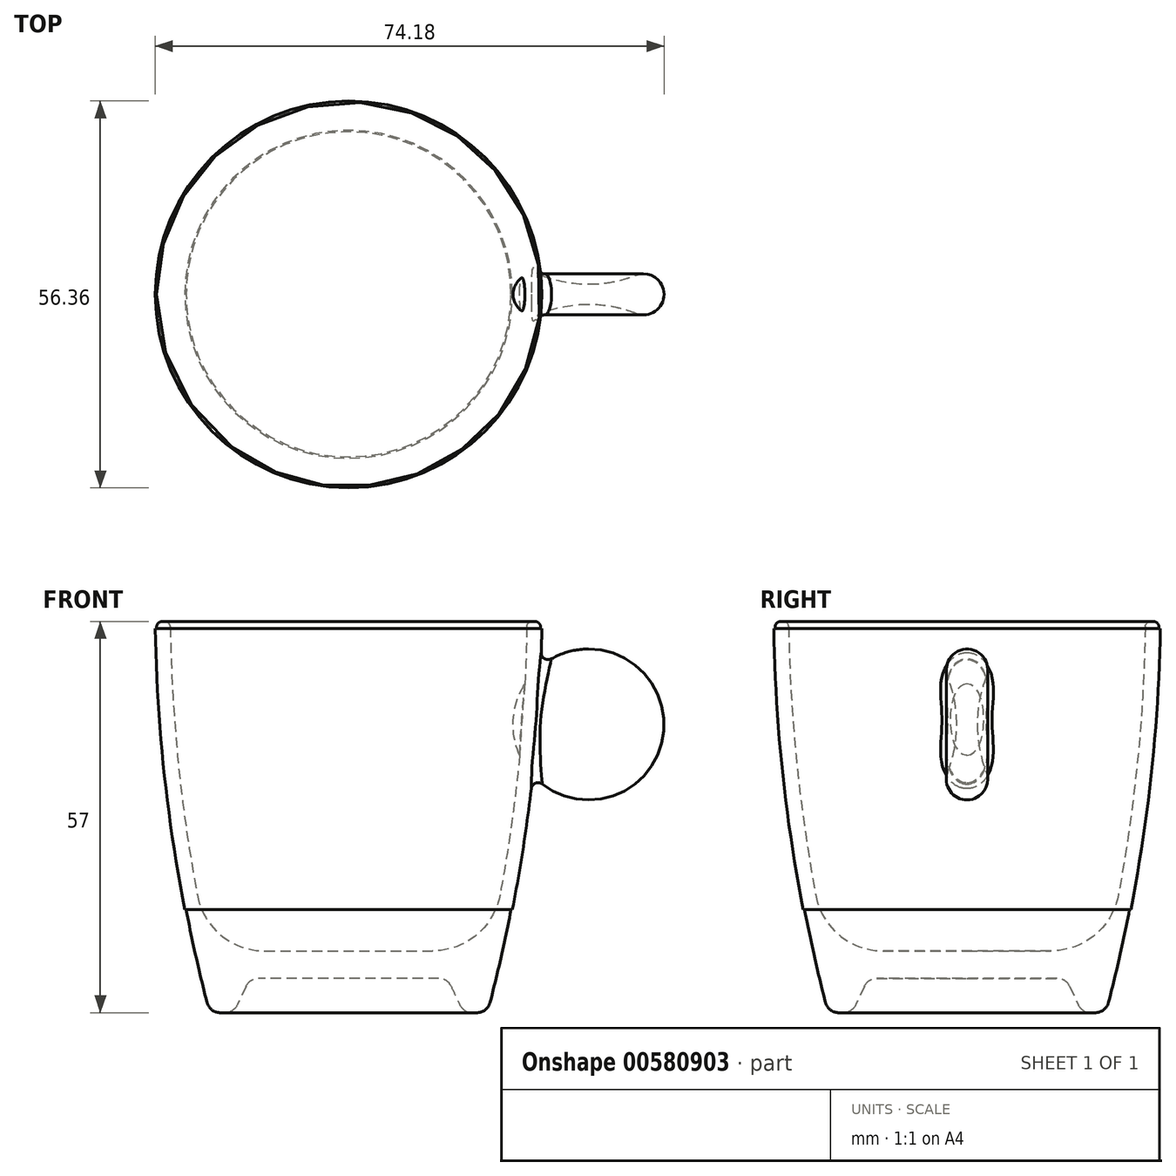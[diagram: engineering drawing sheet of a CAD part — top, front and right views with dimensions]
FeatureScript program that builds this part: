
annotation { "Feature Type Name" : "Feature", "Feature Type Description" : "" }
export const myFeature = defineFeature(function(context is Context, id is Id, definition is map)
    precondition{}
    {
        {
            var Q0;
            Q0=qCreatedBy(makeId("Front.planeOp"),FACE);
            var sketch = newSketch(context, id + "F0", { "sketchPlane" : qUnion([Q0])});
            skLineSegment(sketch, "E0", {"start": v(0, 5) * mm, "end": v(14.42, 5) * mm});
            skLineSegment(sketch, "E1", {"start": v(14.42, 5) * mm, "end": v(16.75, 0) * mm});
            skLineSegment(sketch, "E2", {"start": v(16.75, 0) * mm, "end": v(20.25, 0) * mm});
            skArc(sketch, "E3", {"start": v(20.25, 0) * mm, "mid": v(25.88, 28.26) * mm, "end": v(28, 57) * mm});
            skLineSegment(sketch, "E4", {"start": v(28, 57) * mm, "end": v(26, 57) * mm});
            skLineSegment(sketch, "E5", {"start": v(0, 9) * mm, "end": v(0, 5) * mm});
            skLineSegment(sketch, "E6", {"start": v(20.39, 9) * mm, "end": v(0, 9) * mm});
            skArc(sketch, "E7.trimOffspring", {"start": v(20.39, 9) * mm, "mid": v(24.45, 32.85) * mm, "end": v(26, 57) * mm});
            skPoint(sketch, "E8.orphan", {"position": v(0, 57) * mm});
            skSolve(sketch);
        }
        {
            var Q0;
            Q0=qSketchRegion(id+"F0",true);
            var Q1;
            Q1=sQuery(id+"F0.wireOp",EDGE,"E5");
            revolve(context, id + "F1", {"entities" : qUnion([Q0]), "axis" : qUnion([Q1]), "revolveType" : RevolveType.FULL});
        }
        {
            var Q0;
            Q0=makeQuery(id+"F1.opRevolve","SWEPT_EDGE",EDGE,{"disambiguationData":[OSD([sQuery(id+"F0.wireOp",EDGE,"E4"),sQuery(id+"F0.wireOp",EDGE,"E7.trimOffspring")])]});
            var Q1;
            Q1=makeQuery(id+"F1.opRevolve","SWEPT_EDGE",EDGE,{"disambiguationData":[OSD([sQuery(id+"F0.wireOp",EDGE,"E3"),sQuery(id+"F0.wireOp",EDGE,"E4")])]});
            fillet(context, id + "F2", {"entities" : qUnion([Q0, Q1]), "radius" : .8 * mm, "tangentPropagation" : true, "allowEdgeOverflow" : false});
        }
        {
            var Q0;
            Q0=makeQuery(id+"F1.opRevolve","SWEPT_EDGE",EDGE,{"disambiguationData":[OSD([sQuery(id+"F0.wireOp",EDGE,"E2"),sQuery(id+"F0.wireOp",EDGE,"E3")])]});
            var Q1;
            Q1=makeQuery(id+"F1.opRevolve","SWEPT_EDGE",EDGE,{"disambiguationData":[OSD([sQuery(id+"F0.wireOp",EDGE,"E1"),sQuery(id+"F0.wireOp",EDGE,"E2")])]});
            var Q2;
            Q2=makeQuery(id+"F1.opRevolve","SWEPT_EDGE",EDGE,{"disambiguationData":[OSD([sQuery(id+"F0.wireOp",EDGE,"E0"),sQuery(id+"F0.wireOp",EDGE,"E1")])]});
            fillet(context, id + "F3", {"entities" : qUnion([Q0, Q1, Q2]), "radius" : 2 * mm, "tangentPropagation" : true, "allowEdgeOverflow" : false});
        }
        {
            var Q0;
            Q0=makeQuery(id+"F1.opRevolve","SWEPT_EDGE",EDGE,{"disambiguationData":[OSD([sQuery(id+"F0.wireOp",EDGE,"E6"),sQuery(id+"F0.wireOp",EDGE,"E7.trimOffspring")])]});
            fillet(context, id + "F4", {"entities" : qUnion([Q0]), "radius" : 10 * mm, "tangentPropagation" : true, "allowEdgeOverflow" : false});
        }
        {
            var Q0;
            Q0=qCreatedBy(makeId("Front.planeOp"),FACE);
            var sketch = newSketch(context, id + "F5", { "sketchPlane" : qUnion([Q0])});
            skArc(sketch, "E9", {"start": v(23.7, 15) * mm, "mid": v(26.74, 35.4) * mm, "end": v(27.99, 56) * mm});
            skArc(sketch, "E10", {"start": v(23.9, 15) * mm, "mid": v(26.94, 35.4) * mm, "end": v(28.18, 56) * mm});
            skLineSegment(sketch, "E11", {"start": v(27.99, 56) * mm, "end": v(28.18, 56) * mm});
            skLineSegment(sketch, "E12", {"start": v(23.9, 15) * mm, "end": v(23.7, 15) * mm});
            skSolve(sketch);
        }
        {
            var Q0;
            Q0=makeQuery(id+"F5.imprint","IMPRINT",FACE,{"disambiguationData":[TD([[makeQuery(id+"F5.imprint","IMPRINT",EDGE,{"derivedFrom":sQuery(id+"F5.wireOp",EDGE,"E9")}),-1.0]])]});
            var Q1;
            Q1=sQuery(id+"F0.wireOp",EDGE,"E5");
            revolve(context, id + "F6", {"operationType" : NewBodyOperationType.ADD, "entities" : qUnion([Q0]), "axis" : qUnion([Q1]), "revolveType" : RevolveType.FULL});
        }
        {
            var Q0;
            Q0=makeQuery(id+"F1.opRevolve","SWEPT_FACE",FACE,{"disambiguationData":[OSD([sQuery(id+"F0.wireOp",EDGE,"E4")])]});
            cPlane(context, id + "F7", {"entities" : qUnion([Q0]), "cplaneType" : CPlaneType.OFFSET, "offset" : 15 * mm, "oppositeDirection" : true, "width" : 150 * mm, "height" : 150 * mm});
        }
        {
            var Q0;
            Q0=qCreatedBy(id+"F7.planeOp",FACE);
            var sketch = newSketch(context, id + "F8", { "sketchPlane" : qUnion([Q0])});
            skArc(sketch, "E13", {"start": v(46, 0) * mm, "mid": v(44.7, 2.48) * mm, "end": v(41.91, 2.8) * mm});
            skArc(sketch, "E14", {"start": v(35, 1.5) * mm, "mid": v(38.52, 1.83) * mm, "end": v(41.91, 2.8) * mm});
            skLineSegment(sketch, "E15", {"start": v(35, 1.5) * mm, "end": v(35, 0) * mm});
            skArc(sketch, "E16.MirrorCS", {"start": v(46, 0) * mm, "mid": v(44.7, -2.48) * mm, "end": v(41.91, -2.8) * mm});
            skArc(sketch, "E17.MirrorCS", {"start": v(35, -1.5) * mm, "mid": v(38.52, -1.83) * mm, "end": v(41.91, -2.8) * mm});
            skLineSegment(sketch, "E18.MirrorCS", {"start": v(35, -1.5) * mm, "end": v(35, 0) * mm});
            skSolve(sketch);
        }
        {
            var Q0;
            Q0=makeQuery(id+"F8.imprint","IMPRINT",FACE,{"disambiguationData":[TD([[makeQuery(id+"F8.imprint","IMPRINT",EDGE,{"derivedFrom":sQuery(id+"F8.wireOp",EDGE,"E13")}),1.0]])]});
            var Q1;
            Q1=sQuery(id+"F8.wireOp",EDGE,"E15");
            revolve(context, id + "F9", {"operationType" : NewBodyOperationType.ADD, "entities" : qUnion([Q0]), "axis" : qUnion([Q1]), "revolveType" : RevolveType.FULL});
        }
        {
            var Q0;
            Q0=makeQuery(id+"F9.boolean.opBoolean","INTERSECT",EDGE,{"disambiguationData":[OD(1.0)],"derivedFrom":[makeQuery(id+"F6.opRevolve","SWEPT_FACE",FACE,{"disambiguationData":[OSD([sQuery(id+"F5.wireOp",EDGE,"E10")])]}),makeQuery(id+"F9.opRevolve","SWEPT_FACE",FACE,{"disambiguationData":[OSD([sQuery(id+"F8.wireOp",EDGE,"E13"),sQuery(id+"F8.wireOp",EDGE,"E16.MirrorCS")])]})]});
            var Q1;
            Q1=makeQuery(id+"F9.boolean.opBoolean","INTERSECT",EDGE,{"derivedFrom":[makeQuery(id+"F6.opRevolve","SWEPT_FACE",FACE,{"disambiguationData":[OSD([sQuery(id+"F5.wireOp",EDGE,"E10")])]}),makeQuery(id+"F9.opRevolve","SWEPT_FACE",FACE,{"disambiguationData":[OSD([sQuery(id+"F8.wireOp",EDGE,"E17.MirrorCS")])]})]});
            var Q2;
            Q2=makeQuery(id+"F9.boolean.opBoolean","INTERSECT",EDGE,{"disambiguationData":[OD(0.0)],"derivedFrom":[makeQuery(id+"F6.opRevolve","SWEPT_FACE",FACE,{"disambiguationData":[OSD([sQuery(id+"F5.wireOp",EDGE,"E10")])]}),makeQuery(id+"F9.opRevolve","SWEPT_FACE",FACE,{"disambiguationData":[OSD([sQuery(id+"F8.wireOp",EDGE,"E13"),sQuery(id+"F8.wireOp",EDGE,"E16.MirrorCS")])]})]});
            var Q3;
            Q3=makeQuery(id+"F9.boolean.opBoolean","INTERSECT",EDGE,{"derivedFrom":[makeQuery(id+"F6.opRevolve","SWEPT_FACE",FACE,{"disambiguationData":[OSD([sQuery(id+"F5.wireOp",EDGE,"E10")])]}),makeQuery(id+"F9.opRevolve","SWEPT_FACE",FACE,{"disambiguationData":[OSD([sQuery(id+"F8.wireOp",EDGE,"E14")])]})]});
            fillet(context, id + "F10", {"entities" : qUnion([Q0, Q1, Q2, Q3]), "radius" : 1 * mm, "tangentPropagation" : true, "allowEdgeOverflow" : false});
        }
    });
